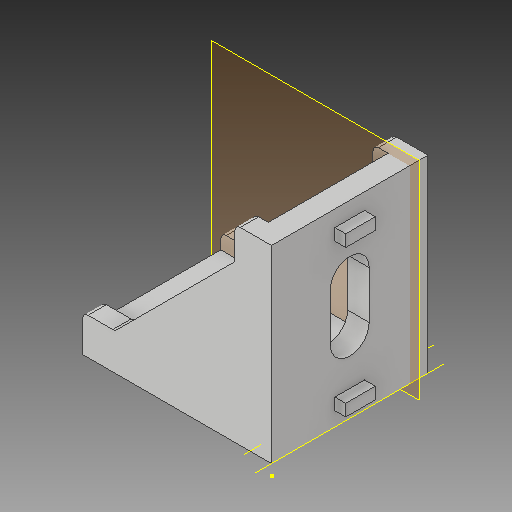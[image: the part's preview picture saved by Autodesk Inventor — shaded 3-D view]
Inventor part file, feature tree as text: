
AUTODESK INVENTOR PART (.ipt)
format: ipt  version: 2017 (Build 210142000, 142)  size: 181,248 bytes
history: native  units: mm
features: sketch x7, other x5, plane x1
ambient origin geometry x8: Origin, YZ Plane, XZ Plane, XY Plane, X Axis, Y Axis, Z Axis, Center Point
bodies: Solid1 (feature_tree)
feature tree (13):
  other  "30mm Bracket.ipt"
  other  "Solid1::30mm Bracket.ipt"
  other  "TaggingFeature1"
  sketch  "Sketch1"  dims[d0=10.0mm]
  sketch  "Sketch2"
  sketch  "Sketch3"
  sketch  "Sketch4"
  sketch  "Sketch5"
  sketch  "Sketch7"
  sketch  "Sketch9"
  plane  "Work Plane1"
  other  "Work Axis1"
  other  "Work Axis2"
